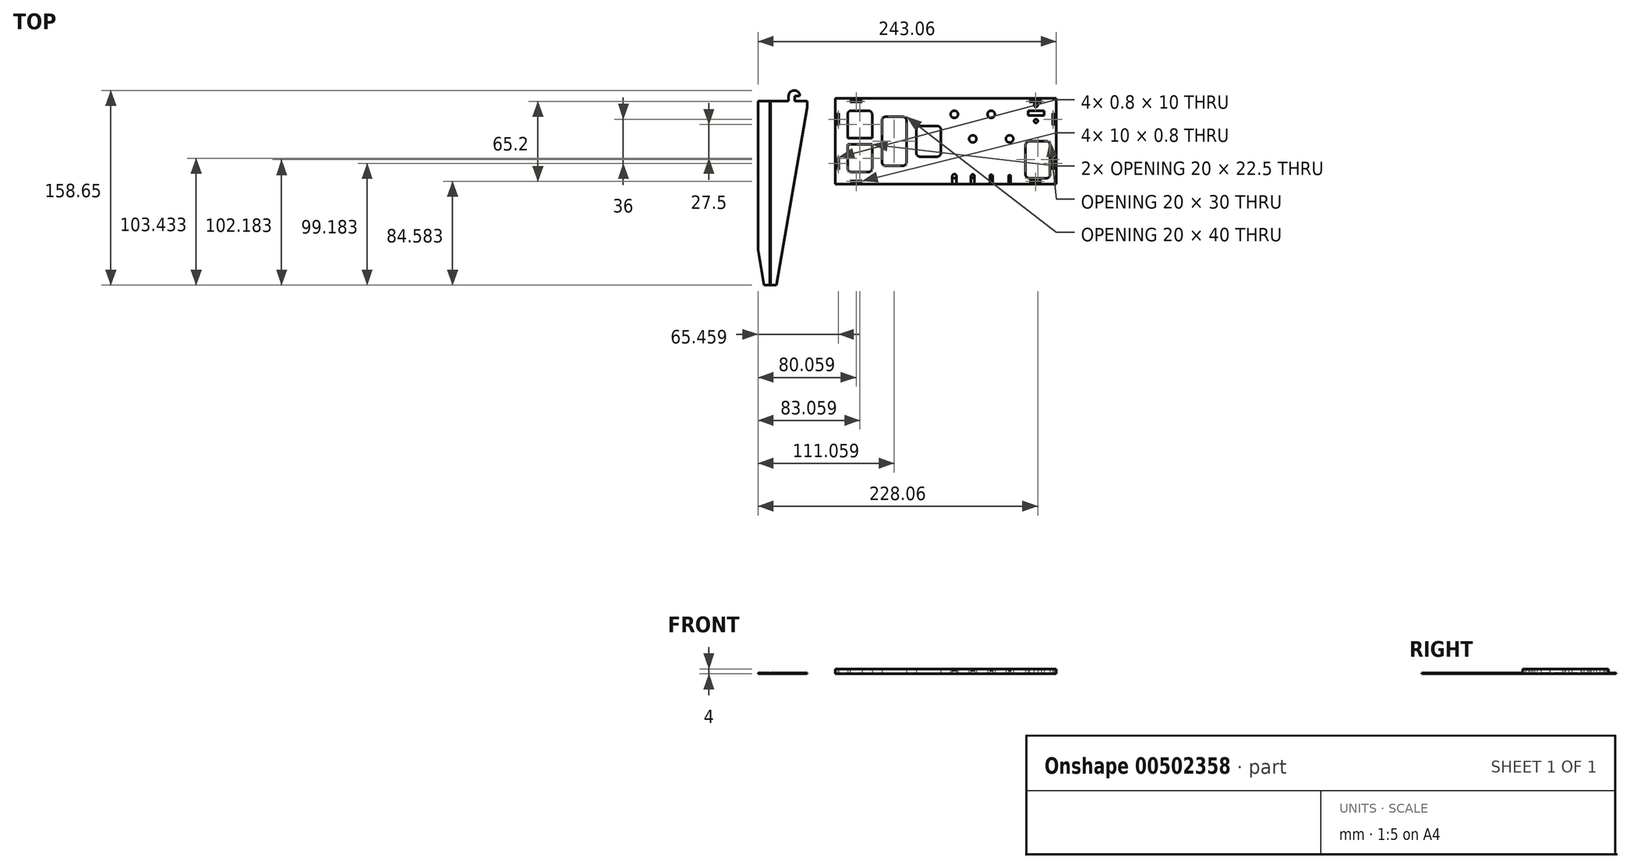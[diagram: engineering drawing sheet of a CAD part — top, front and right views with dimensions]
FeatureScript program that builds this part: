
annotation { "Feature Type Name" : "Feature", "Feature Type Description" : "" }
export const myFeature = defineFeature(function(context is Context, id is Id, definition is map)
    precondition{}
    {
        {
            var Q0;
            Q0=qCreatedBy(makeId("Top.planeOp"),FACE);
            var sketch = newSketch(context, id + "F0", { "sketchPlane" : qUnion([Q0])});
            skLineSegment(sketch, "E0.bottom", {"start": v(-80.88, 36.58) * mm, "end": v(-66.88, 36.58) * mm});
            skLineSegment(sketch, "E0.top", {"start": v(-80.88, -13.42) * mm, "end": v(-66.88, -13.42) * mm});
            skLineSegment(sketch, "E0.left", {"start": v(-83.88, 33.58) * mm, "end": v(-83.88, -10.42) * mm});
            skLineSegment(sketch, "E0.right", {"start": v(-63.88, 33.58) * mm, "end": v(-63.88, -10.42) * mm});
            skLineSegment(sketch, "E1.bottom", {"start": v(-52.88, 31.58) * mm, "end": v(-38.88, 31.58) * mm});
            skLineSegment(sketch, "E1.top", {"start": v(-52.88, -8.42) * mm, "end": v(-38.88, -8.42) * mm});
            skLineSegment(sketch, "E1.left", {"start": v(-55.88, 28.58) * mm, "end": v(-55.88, -5.42) * mm});
            skLineSegment(sketch, "E1.right", {"start": v(-35.88, 28.58) * mm, "end": v(-35.88, -5.42) * mm});
            skLineSegment(sketch, "E2.bottom", {"start": v(-24.88, 24.08) * mm, "end": v(-10.88, 24.08) * mm});
            skLineSegment(sketch, "E2.top", {"start": v(-24.88, -0.92) * mm, "end": v(-10.88, -0.92) * mm});
            skLineSegment(sketch, "E2.left", {"start": v(-27.88, 21.08) * mm, "end": v(-27.88, 2.08) * mm});
            skLineSegment(sketch, "E2.right", {"start": v(-7.88, 21.08) * mm, "end": v(-7.88, 2.08) * mm});
            skLineSegment(sketch, "E3.bottom", {"start": v(-93.88, 46.58) * mm, "end": v(86.12, 46.58) * mm});
            skLineSegment(sketch, "E3.top", {"start": v(-93.88, -23.42) * mm, "end": v(86.12, -23.42) * mm});
            skLineSegment(sketch, "E3.left", {"start": v(-93.88, 46.58) * mm, "end": v(-93.88, -23.42) * mm});
            skLineSegment(sketch, "E3.right", {"start": v(86.12, 46.58) * mm, "end": v(86.12, -23.42) * mm});
            skPoint(sketch, "E4", {"position": v(-63.88, 11.58) * mm});
            skPoint(sketch, "E5", {"position": v(-35.88, 11.58) * mm});
            skPoint(sketch, "E6", {"position": v(-7.88, 11.58) * mm});
            skCircle(sketch, "E7", {"center": v(3.12, 33.58) * mm, "radius": 3 * mm});
            skCircle(sketch, "E8", {"center": v(33.12, 33.58) * mm, "radius": 3 * mm});
            skCircle(sketch, "E9", {"center": v(18.12, 13.58) * mm, "radius": 3 * mm});
            skCircle(sketch, "E10", {"center": v(48.12, 13.58) * mm, "radius": 3 * mm});
            skLineSegment(sketch, "E11.bottom", {"start": v(-63.88, 14.08) * mm, "end": v(-83.88, 14.08) * mm});
            skLineSegment(sketch, "E11.top", {"start": v(-63.88, 9.08) * mm, "end": v(-83.88, 9.08) * mm});
            skLineSegment(sketch, "E11.left", {"start": v(-63.88, 14.08) * mm, "end": v(-63.88, 9.08) * mm});
            skLineSegment(sketch, "E11.right", {"start": v(-83.88, 14.08) * mm, "end": v(-83.88, 9.08) * mm});
            skLineSegment(sketch, "E12", {"start": v(3.12, 46.58) * mm, "end": v(3.12, -23.42) * mm, "construction": true});
            skLineSegment(sketch, "E13", {"start": v(18.12, 46.58) * mm, "end": v(18.12, -23.42) * mm, "construction": true});
            skLineSegment(sketch, "E14", {"start": v(33.12, 46.58) * mm, "end": v(33.12, -23.42) * mm, "construction": true});
            skLineSegment(sketch, "E15", {"start": v(48.12, 46.58) * mm, "end": v(48.12, -23.42) * mm, "construction": true});
            skLineSegment(sketch, "E16.bottom", {"start": v(63.12, 36.58) * mm, "end": v(76.12, 36.58) * mm});
            skLineSegment(sketch, "E16.top", {"start": v(63.12, 32.58) * mm, "end": v(76.12, 32.58) * mm});
            skLineSegment(sketch, "E16.left", {"start": v(63.12, 36.58) * mm, "end": v(63.12, 32.58) * mm});
            skLineSegment(sketch, "E16.right", {"start": v(76.12, 36.58) * mm, "end": v(76.12, 32.58) * mm});
            skCircle(sketch, "E17", {"center": v(69.62, 41.08) * mm, "radius": 1.5 * mm});
            skPoint(sketch, "E17.centerSnap0", {"position": v(69.62, 36.58) * mm});
            skCircle(sketch, "E18", {"center": v(69.62, 28.08) * mm, "radius": 1.5 * mm});
            skPoint(sketch, "E19.visualSharp", {"position": v(-83.88, 36.58) * mm});
            skArc(sketch, "E19.filletArc", {"start": v(-80.88, 36.58) * mm, "mid": v(-83, 35.7) * mm, "end": v(-83.88, 33.58) * mm});
            skPoint(sketch, "E20.visualSharp", {"position": v(-83.88, -13.42) * mm});
            skArc(sketch, "E20.filletArc", {"start": v(-83.88, -10.42) * mm, "mid": v(-83, -12.54) * mm, "end": v(-80.88, -13.42) * mm});
            skPoint(sketch, "E21.visualSharp", {"position": v(-63.88, -13.42) * mm});
            skArc(sketch, "E21.filletArc", {"start": v(-66.88, -13.42) * mm, "mid": v(-64.76, -12.54) * mm, "end": v(-63.88, -10.42) * mm});
            skPoint(sketch, "E22.visualSharp", {"position": v(-63.88, 36.58) * mm});
            skArc(sketch, "E22.filletArc", {"start": v(-63.88, 33.58) * mm, "mid": v(-64.76, 35.7) * mm, "end": v(-66.88, 36.58) * mm});
            skPoint(sketch, "E23.visualSharp", {"position": v(-55.88, 31.58) * mm});
            skArc(sketch, "E23.filletArc", {"start": v(-52.88, 31.58) * mm, "mid": v(-55, 30.7) * mm, "end": v(-55.88, 28.58) * mm});
            skPoint(sketch, "E24.visualSharp", {"position": v(-55.88, -8.42) * mm});
            skArc(sketch, "E24.filletArc", {"start": v(-55.88, -5.42) * mm, "mid": v(-55, -7.54) * mm, "end": v(-52.88, -8.42) * mm});
            skPoint(sketch, "E25.visualSharp", {"position": v(-35.88, -8.42) * mm});
            skArc(sketch, "E25.filletArc", {"start": v(-38.88, -8.42) * mm, "mid": v(-36.76, -7.54) * mm, "end": v(-35.88, -5.42) * mm});
            skPoint(sketch, "E26.visualSharp", {"position": v(-35.88, 31.58) * mm});
            skArc(sketch, "E26.filletArc", {"start": v(-35.88, 28.58) * mm, "mid": v(-36.76, 30.7) * mm, "end": v(-38.88, 31.58) * mm});
            skPoint(sketch, "E27.visualSharp", {"position": v(-27.88, 24.08) * mm});
            skArc(sketch, "E27.filletArc", {"start": v(-24.88, 24.08) * mm, "mid": v(-27, 23.2) * mm, "end": v(-27.88, 21.08) * mm});
            skPoint(sketch, "E28.visualSharp", {"position": v(-27.88, -0.92) * mm});
            skArc(sketch, "E28.filletArc", {"start": v(-27.88, 2.08) * mm, "mid": v(-27, -0.04) * mm, "end": v(-24.88, -0.92) * mm});
            skPoint(sketch, "E29.visualSharp", {"position": v(-7.88, 24.08) * mm});
            skArc(sketch, "E29.filletArc", {"start": v(-7.88, 21.08) * mm, "mid": v(-8.76, 23.2) * mm, "end": v(-10.88, 24.08) * mm});
            skPoint(sketch, "E30.visualSharp", {"position": v(-7.88, -0.92) * mm});
            skArc(sketch, "E30.filletArc", {"start": v(-10.88, -0.92) * mm, "mid": v(-8.76, -0.04) * mm, "end": v(-7.88, 2.08) * mm});
            skLineSegment(sketch, "E31.bottom", {"start": v(-133.26, 88) * mm, "end": v(-148.26, 88) * mm});
            skLineSegment(sketch, "E31.top", {"start": v(-133.26, 103) * mm, "end": v(-142.1, 103) * mm});
            skLineSegment(sketch, "E31.left", {"start": v(-133.26, 88) * mm, "end": v(-133.26, 103) * mm});
            skLineSegment(sketch, "E31.right", {"start": v(-148.26, 88) * mm, "end": v(-148.26, 96.85) * mm});
            skPoint(sketch, "E31.middle", {"position": v(-140.76, 95.5) * mm});
            skLineSegment(sketch, "E32.bottom", {"start": v(-145.76, 90.5) * mm, "end": v(-135.76, 90.5) * mm});
            skLineSegment(sketch, "E32.top", {"start": v(-137.76, 100.5) * mm, "end": v(-135.76, 100.5) * mm});
            skLineSegment(sketch, "E32.left", {"start": v(-145.76, 90.5) * mm, "end": v(-145.76, 92.5) * mm});
            skLineSegment(sketch, "E32.right", {"start": v(-135.76, 90.5) * mm, "end": v(-135.76, 100.5) * mm});
            skPoint(sketch, "E33.visualSharp", {"position": v(-145.76, 100.5) * mm});
            skArc(sketch, "E33.filletArc", {"start": v(-137.76, 100.5) * mm, "mid": v(-143.41, 98.16) * mm, "end": v(-145.76, 92.5) * mm});
            skPoint(sketch, "E34.visualSharp", {"position": v(-148.26, 103) * mm});
            skArc(sketch, "E34.filletArc", {"start": v(-142.1, 103) * mm, "mid": v(-146.45, 101.2) * mm, "end": v(-148.26, 96.85) * mm});
            skLineSegment(sketch, "E35.bottom", {"start": v(-81.88, 44.58) * mm, "end": v(-71.88, 44.58) * mm});
            skLineSegment(sketch, "E35.top", {"start": v(-81.88, 43.78) * mm, "end": v(-71.88, 43.78) * mm});
            skLineSegment(sketch, "E35.left", {"start": v(-81.88, 44.58) * mm, "end": v(-81.88, 43.78) * mm});
            skLineSegment(sketch, "E35.right", {"start": v(-71.88, 44.58) * mm, "end": v(-71.88, 43.78) * mm});
            skLineSegment(sketch, "E36.bottom", {"start": v(-91.88, 34.58) * mm, "end": v(-91.08, 34.58) * mm});
            skLineSegment(sketch, "E36.top", {"start": v(-91.88, 24.58) * mm, "end": v(-91.08, 24.58) * mm});
            skLineSegment(sketch, "E36.left", {"start": v(-91.88, 34.58) * mm, "end": v(-91.88, 24.58) * mm});
            skLineSegment(sketch, "E36.right", {"start": v(-91.08, 34.58) * mm, "end": v(-91.08, 24.58) * mm});
            skLineSegment(sketch, "E37", {"start": v(-91.88, 34.58) * mm, "end": v(-91.88, 44.58) * mm, "construction": true});
            skLineSegment(sketch, "E38", {"start": v(-81.88, 44.58) * mm, "end": v(-91.88, 44.58) * mm, "construction": true});
            skLineSegment(sketch, "E39", {"start": v(-146.94, 44.4) * mm, "end": v(-136.94, 44.4) * mm});
            skLineSegment(sketch, "E40", {"start": v(-136.94, 44.4) * mm, "end": v(-131.94, 44.4) * mm});
            skLineSegment(sketch, "E41", {"start": v(-131.94, 44.4) * mm, "end": v(-131.94, 48.4) * mm});
            skLineSegment(sketch, "E42", {"start": v(-131.94, 48.4) * mm, "end": v(-126.94, 48.4) * mm});
            skLineSegment(sketch, "E43", {"start": v(-126.94, 48.4) * mm, "end": v(-126.94, 44.4) * mm});
            skLineSegment(sketch, "E44", {"start": v(-126.94, 44.4) * mm, "end": v(-116.94, 44.4) * mm});
            skLineSegment(sketch, "E45", {"start": v(-116.94, 44.4) * mm, "end": v(-116.94, 39.4) * mm});
            skLineSegment(sketch, "E46", {"start": v(-146.94, 44.4) * mm, "end": v(-146.94, -105.6) * mm});
            skLineSegment(sketch, "E47", {"start": v(-146.94, -105.6) * mm, "end": v(-141.94, -105.6) * mm});
            skLineSegment(sketch, "E48", {"start": v(-141.94, -105.6) * mm, "end": v(-116.94, 39.4) * mm});
            skArc(sketch, "E49", {"start": v(-131.94, 48.4) * mm, "mid": v(-127.29, 53.05) * mm, "end": v(-122.64, 48.4) * mm});
            skLineSegment(sketch, "E50", {"start": v(-122.64, 48.4) * mm, "end": v(-126.94, 48.4) * mm});
            skLineSegment(sketch, "E51", {"start": v(-136.94, 44.4) * mm, "end": v(-136.94, -76.6) * mm});
            skLineSegment(sketch, "E52", {"start": v(-122.66, 48.87) * mm, "end": v(-123.94, 48.4) * mm});
            skCircle(sketch, "E53", {"center": v(3.12, -16.77) * mm, "radius": 1.65 * mm});
            skCircle(sketch, "E54", {"center": v(18.12, -16.77) * mm, "radius": 1.4 * mm});
            skCircle(sketch, "E55", {"center": v(33.12, -16.77) * mm, "radius": 1.15 * mm});
            skCircle(sketch, "E56", {"center": v(48.12, -16.77) * mm, "radius": 0.9 * mm});
            skLineSegment(sketch, "E57", {"start": v(1.47, -16.77) * mm, "end": v(1.47, -23.42) * mm});
            skLineSegment(sketch, "E58", {"start": v(4.77, -16.77) * mm, "end": v(4.77, -23.42) * mm});
            skLineSegment(sketch, "E59", {"start": v(16.72, -16.77) * mm, "end": v(16.72, -23.42) * mm});
            skLineSegment(sketch, "E60", {"start": v(19.52, -16.77) * mm, "end": v(19.52, -23.42) * mm});
            skLineSegment(sketch, "E61", {"start": v(31.97, -16.77) * mm, "end": v(31.97, -23.42) * mm});
            skLineSegment(sketch, "E62", {"start": v(34.27, -16.77) * mm, "end": v(34.27, -23.42) * mm});
            skLineSegment(sketch, "E63", {"start": v(47.22, -16.77) * mm, "end": v(47.22, -23.42) * mm});
            skLineSegment(sketch, "E64", {"start": v(49.02, -16.77) * mm, "end": v(49.02, -23.42) * mm});
            skLineSegment(sketch, "E65.bottom", {"start": v(86.12, 36.58) * mm, "end": v(101.12, 36.58) * mm});
            skLineSegment(sketch, "E65.top", {"start": v(86.12, 30.58) * mm, "end": v(101.12, 30.58) * mm});
            skLineSegment(sketch, "E65.left", {"start": v(86.12, 36.58) * mm, "end": v(86.12, 30.58) * mm});
            skLineSegment(sketch, "E65.right", {"start": v(101.12, 36.58) * mm, "end": v(101.12, 30.58) * mm});
            skLineSegment(sketch, "E66.bottom", {"start": v(86.12, -7.42) * mm, "end": v(101.12, -7.42) * mm});
            skLineSegment(sketch, "E66.top", {"start": v(86.12, -13.42) * mm, "end": v(101.12, -13.42) * mm});
            skLineSegment(sketch, "E66.left", {"start": v(86.12, -7.42) * mm, "end": v(86.12, -13.42) * mm});
            skLineSegment(sketch, "E66.right", {"start": v(101.12, -7.42) * mm, "end": v(101.12, -13.42) * mm});
            skLineSegment(sketch, "E67.bottom", {"start": v(101.12, 30.58) * mm, "end": v(97.12, 30.58) * mm});
            skLineSegment(sketch, "E67.top", {"start": v(101.12, 36.58) * mm, "end": v(97.12, 36.58) * mm});
            skLineSegment(sketch, "E67.left", {"start": v(101.12, 30.58) * mm, "end": v(101.12, 36.58) * mm});
            skLineSegment(sketch, "E67.right", {"start": v(97.12, 30.58) * mm, "end": v(97.12, 36.58) * mm});
            skLineSegment(sketch, "E68.bottom", {"start": v(101.12, -13.42) * mm, "end": v(97.12, -13.42) * mm});
            skLineSegment(sketch, "E68.top", {"start": v(101.12, -7.42) * mm, "end": v(97.12, -7.42) * mm});
            skLineSegment(sketch, "E68.left", {"start": v(101.12, -13.42) * mm, "end": v(101.12, -7.42) * mm});
            skLineSegment(sketch, "E68.right", {"start": v(97.12, -13.42) * mm, "end": v(97.12, -7.42) * mm});
            skLineSegment(sketch, "E69.bottom", {"start": v(64.12, 11.58) * mm, "end": v(78.12, 11.58) * mm});
            skLineSegment(sketch, "E69.top", {"start": v(64.12, -18.42) * mm, "end": v(78.12, -18.42) * mm});
            skLineSegment(sketch, "E69.left", {"start": v(61.12, 8.58) * mm, "end": v(61.12, -15.42) * mm});
            skLineSegment(sketch, "E69.right", {"start": v(81.12, 8.58) * mm, "end": v(81.12, -15.42) * mm});
            skPoint(sketch, "E70.visualSharp", {"position": v(61.12, 11.58) * mm});
            skArc(sketch, "E70.filletArc", {"start": v(64.12, 11.58) * mm, "mid": v(62, 10.7) * mm, "end": v(61.12, 8.58) * mm});
            skPoint(sketch, "E71.visualSharp", {"position": v(81.12, -18.42) * mm});
            skArc(sketch, "E71.filletArc", {"start": v(78.12, -18.42) * mm, "mid": v(80.24, -17.54) * mm, "end": v(81.12, -15.42) * mm});
            skPoint(sketch, "E72.visualSharp", {"position": v(81.12, 11.58) * mm});
            skArc(sketch, "E72.filletArc", {"start": v(81.12, 8.58) * mm, "mid": v(80.24, 10.7) * mm, "end": v(78.12, 11.58) * mm});
            skPoint(sketch, "E73.visualSharp", {"position": v(61.12, -18.42) * mm});
            skArc(sketch, "E73.filletArc", {"start": v(61.12, -15.42) * mm, "mid": v(62, -17.54) * mm, "end": v(64.12, -18.42) * mm});
            skLineSegment(sketch, "E74.0.1.0", {"start": v(-91.88, -1.42) * mm, "end": v(-91.08, -1.42) * mm});
            skLineSegment(sketch, "E74.0.1.1", {"start": v(-91.08, -1.42) * mm, "end": v(-91.08, -11.42) * mm});
            skLineSegment(sketch, "E74.0.1.2", {"start": v(-91.88, -1.42) * mm, "end": v(-91.88, 8.58) * mm, "construction": true});
            skLineSegment(sketch, "E74.0.1.3", {"start": v(-91.88, -1.42) * mm, "end": v(-91.88, -11.42) * mm});
            skLineSegment(sketch, "E74.0.1.4", {"start": v(-91.88, -11.42) * mm, "end": v(-91.08, -11.42) * mm});
            skLineSegment(sketch, "E74.1.0.0", {"start": v(83.32, 34.58) * mm, "end": v(84.12, 34.58) * mm});
            skLineSegment(sketch, "E74.1.0.1", {"start": v(84.12, 34.58) * mm, "end": v(84.12, 24.58) * mm});
            skLineSegment(sketch, "E74.1.0.2", {"start": v(83.32, 34.58) * mm, "end": v(83.32, 44.58) * mm, "construction": true});
            skLineSegment(sketch, "E74.1.0.3", {"start": v(83.32, 34.58) * mm, "end": v(83.32, 24.58) * mm});
            skLineSegment(sketch, "E74.1.0.4", {"start": v(83.32, 24.58) * mm, "end": v(84.12, 24.58) * mm});
            skLineSegment(sketch, "E74.1.1.0", {"start": v(83.32, -1.42) * mm, "end": v(84.12, -1.42) * mm});
            skLineSegment(sketch, "E74.1.1.1", {"start": v(84.12, -1.42) * mm, "end": v(84.12, -11.42) * mm});
            skLineSegment(sketch, "E74.1.1.2", {"start": v(83.32, -1.42) * mm, "end": v(83.32, 8.58) * mm, "construction": true});
            skLineSegment(sketch, "E74.1.1.3", {"start": v(83.32, -1.42) * mm, "end": v(83.32, -11.42) * mm});
            skLineSegment(sketch, "E74.1.1.4", {"start": v(83.32, -11.42) * mm, "end": v(84.12, -11.42) * mm});
            skLineSegment(sketch, "E74.direction1", {"start": v(-91.88, 24.58) * mm, "end": v(83.32, 24.58) * mm, "construction": true});
            skLineSegment(sketch, "E74.direction2", {"start": v(-91.88, 24.58) * mm, "end": v(-91.88, -11.42) * mm, "construction": true});
            skLineSegment(sketch, "E75.0.1.0", {"start": v(-81.88, -20.62) * mm, "end": v(-81.88, -21.42) * mm});
            skLineSegment(sketch, "E75.0.1.1", {"start": v(-81.88, -20.62) * mm, "end": v(-71.88, -20.62) * mm});
            skLineSegment(sketch, "E75.0.1.2", {"start": v(-71.88, -20.62) * mm, "end": v(-71.88, -21.42) * mm});
            skLineSegment(sketch, "E75.0.1.3", {"start": v(-81.88, -21.42) * mm, "end": v(-71.88, -21.42) * mm});
            skLineSegment(sketch, "E75.1.0.0", {"start": v(64.12, 44.58) * mm, "end": v(64.12, 43.78) * mm});
            skLineSegment(sketch, "E75.1.0.1", {"start": v(64.12, 44.58) * mm, "end": v(74.12, 44.58) * mm});
            skLineSegment(sketch, "E75.1.0.2", {"start": v(74.12, 44.58) * mm, "end": v(74.12, 43.78) * mm});
            skLineSegment(sketch, "E75.1.0.3", {"start": v(64.12, 43.78) * mm, "end": v(74.12, 43.78) * mm});
            skLineSegment(sketch, "E75.1.1.0", {"start": v(64.12, -20.62) * mm, "end": v(64.12, -21.42) * mm});
            skLineSegment(sketch, "E75.1.1.1", {"start": v(64.12, -20.62) * mm, "end": v(74.12, -20.62) * mm});
            skLineSegment(sketch, "E75.1.1.2", {"start": v(74.12, -20.62) * mm, "end": v(74.12, -21.42) * mm});
            skLineSegment(sketch, "E75.1.1.3", {"start": v(64.12, -21.42) * mm, "end": v(74.12, -21.42) * mm});
            skLineSegment(sketch, "E75.direction1", {"start": v(-81.88, 43.78) * mm, "end": v(64.12, 43.78) * mm, "construction": true});
            skLineSegment(sketch, "E75.direction2", {"start": v(-81.88, 43.78) * mm, "end": v(-81.88, -21.42) * mm, "construction": true});
            skLineSegment(sketch, "E76", {"start": v(-91.88, -11.42) * mm, "end": v(-91.88, -21.42) * mm, "construction": true});
            skLineSegment(sketch, "E77", {"start": v(-91.88, -21.42) * mm, "end": v(-81.88, -21.42) * mm, "construction": true});
            skLineSegment(sketch, "E78", {"start": v(74.12, -21.42) * mm, "end": v(84.12, -21.42) * mm, "construction": true});
            skLineSegment(sketch, "E79", {"start": v(84.12, -21.42) * mm, "end": v(84.12, -11.42) * mm, "construction": true});
            skSolve(sketch);
        }
        {
            var Q0;
            Q0=makeQuery(id+"F0.imprint","IMPRINT",FACE,{"disambiguationData":[TD([[makeQuery(id+"F0.imprint","IMPRINT",EDGE,{"derivedFrom":sQuery(id+"F0.wireOp",EDGE,"E0.bottom")}),1.0]])]});
            var Q1;
            Q1=makeQuery(id+"F0.imprint","IMPRINT",FACE,{"disambiguationData":[TD([[makeQuery(id+"F0.imprint","IMPRINT",EDGE,{"derivedFrom":sQuery(id+"F0.wireOp",EDGE,"E11.bottom")}),1.0]])]});
            extrude(context, id + "F1", {"entities" : qUnion([Q0, Q1]), "depth" : 4 * mm});
        }
        {
            var Q0;
            Q0=makeQuery(id+"F0.imprint","IMPRINT",FACE,{"disambiguationData":[TD([[makeQuery(id+"F0.imprint","IMPRINT",EDGE,{"derivedFrom":sQuery(id+"F0.wireOp",EDGE,"E39")}),-1.0]])]});
            extrude(context, id + "F2", {"entities" : qUnion([Q0]), "depth" : .6 * mm});
        }
        {
            var Q0;
            Q0=makeQuery(id+"F0.imprint","IMPRINT",FACE,{"disambiguationData":[TD([[makeQuery(id+"F0.imprint","IMPRINT",EDGE,{"derivedFrom":sQuery(id+"F0.wireOp",EDGE,"E40")}),-1.0]])]});
            var Q1;
            Q1=makeQuery(id+"F0.imprint","IMPRINT",FACE,{"disambiguationData":[TD([[makeQuery(id+"F0.imprint","IMPRINT",EDGE,{"derivedFrom":sQuery(id+"F0.wireOp",EDGE,"E42")}),1.0]])]});
            extrude(context, id + "F3", {"entities" : qUnion([Q0, Q1]), "depth" : .6 * mm});
        }
        {
            var Q0;
            Q0=makeQuery(id+"F2.opExtrude","CAP_EDGE",EDGE,{"disambiguationData":[OSD([sQuery(id+"F0.wireOp",EDGE,"E46")])],"isStart":false});
            chamfer(context, id + "F4", {"entities" : qUnion([Q0]), "width" : .4 * mm, "tangentPropagation" : true});
        }
        {
            var Q0;
            Q0=makeQuery(id+"F2.opExtrude","SWEPT_BODY",BODY,{"disambiguationData":[OSD([sQuery(id+"F0.wireOp",EDGE,"E39"),sQuery(id+"F0.wireOp",EDGE,"E46"),sQuery(id+"F0.wireOp",EDGE,"E47"),sQuery(id+"F0.wireOp",EDGE,"E48"),sQuery(id+"F0.wireOp",EDGE,"E51")])]});
            var Q1;
            Q1=makeQuery(id+"F2.opExtrude","SWEPT_FACE",FACE,{"disambiguationData":[OSD([sQuery(id+"F0.wireOp",EDGE,"E46")])]});
            mirror(context, id + "F5", {"operationType" : NewBodyOperationType.ADD, "entities" : qUnion([Q0]), "mirrorPlane" : qUnion([Q1])});
        }
        {
            var Q0;
            {var subQ0=sQuery(id+"F0.wireOp",EDGE,"E57");Q0=makeQuery(id+"F0.imprint","IMPRINT",FACE,{"disambiguationData":[TD([[makeQuery(id+"F0.imprint","IMPRINT",EDGE,{"derivedFrom":subQ0}),1.0]])]});}
            var Q1;
            {var subQ0=sQuery(id+"F0.wireOp",EDGE,"E59");Q1=makeQuery(id+"F0.imprint","IMPRINT",FACE,{"disambiguationData":[TD([[makeQuery(id+"F0.imprint","IMPRINT",EDGE,{"derivedFrom":subQ0}),1.0]])]});}
            var Q2;
            {var subQ0=sQuery(id+"F0.wireOp",EDGE,"E61");Q2=makeQuery(id+"F0.imprint","IMPRINT",FACE,{"disambiguationData":[TD([[makeQuery(id+"F0.imprint","IMPRINT",EDGE,{"derivedFrom":subQ0}),1.0]])]});}
            var Q3;
            {var subQ0=sQuery(id+"F0.wireOp",EDGE,"E63");Q3=makeQuery(id+"F0.imprint","IMPRINT",FACE,{"disambiguationData":[TD([[makeQuery(id+"F0.imprint","IMPRINT",EDGE,{"derivedFrom":subQ0}),1.0]])]});}
            extrude(context, id + "F6", {"entities" : qUnion([Q0, Q1, Q2, Q3]), "operationType" : NewBodyOperationType.ADD, "depth" : 3 * mm});
        }
    });
